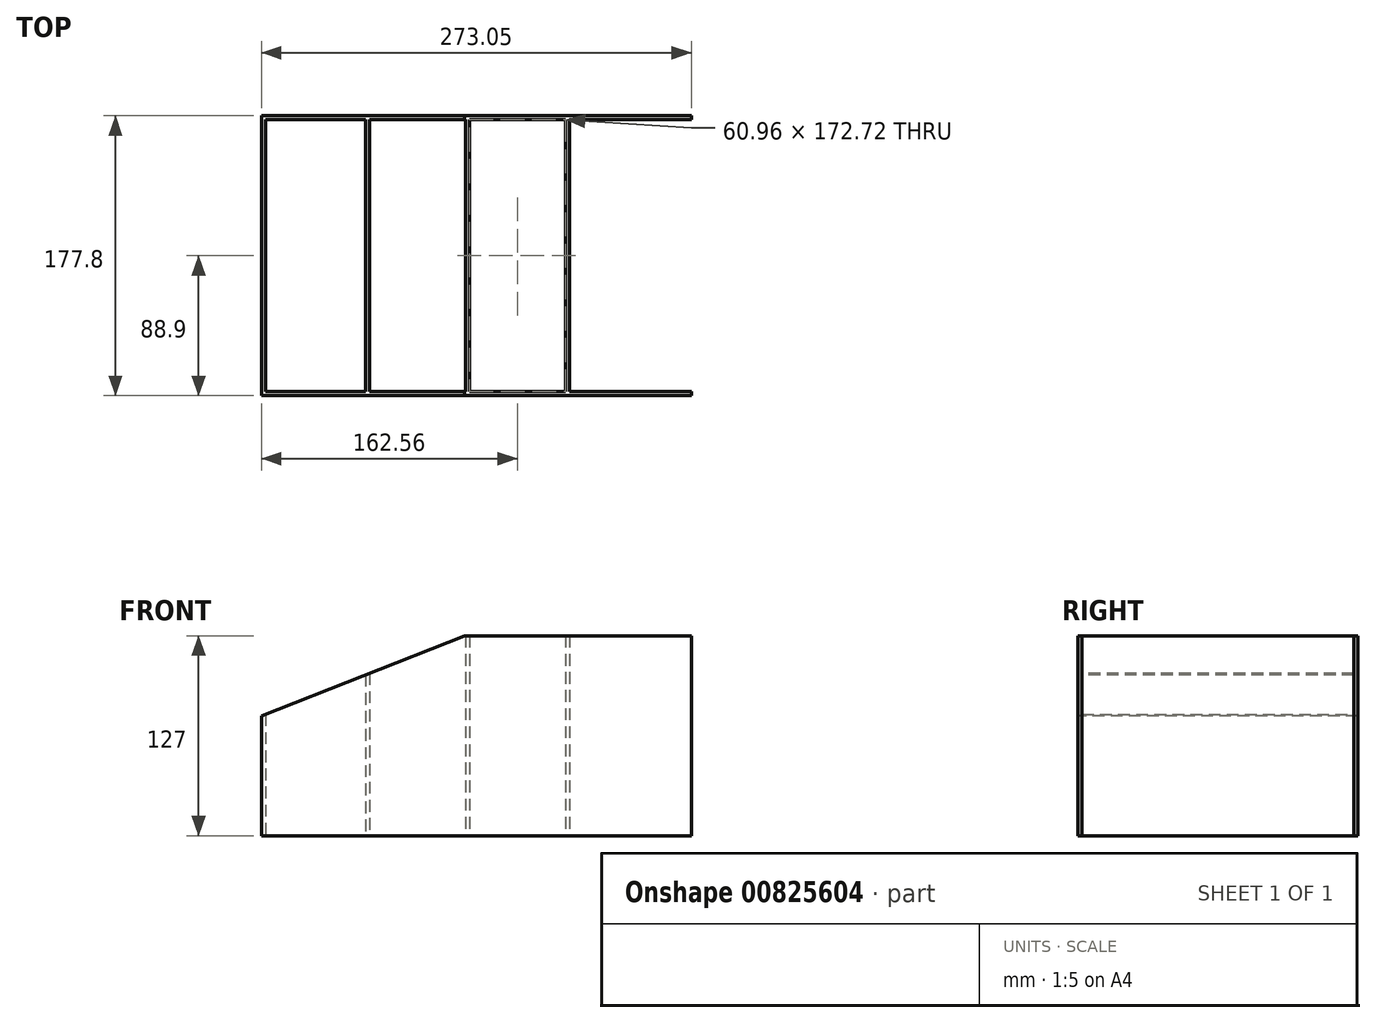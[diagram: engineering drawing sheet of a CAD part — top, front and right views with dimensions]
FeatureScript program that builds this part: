
annotation { "Feature Type Name" : "Feature", "Feature Type Description" : "" }
export const myFeature = defineFeature(function(context is Context, id is Id, definition is map)
    precondition{}
    {
        {
            var Q0;
            Q0=qCreatedBy(makeId("Top.planeOp"),FACE);
            var sketch = newSketch(context, id + "F0", { "sketchPlane" : qUnion([Q0])});
            skLineSegment(sketch, "E0.bottom", {"start": v(0, 0) * mm, "end": v(273.05, 0) * mm});
            skLineSegment(sketch, "E0.top", {"start": v(0, 177.8) * mm, "end": v(273.05, 177.8) * mm});
            skLineSegment(sketch, "E0.left", {"start": v(0, 0) * mm, "end": v(0, 177.8) * mm});
            skLineSegment(sketch, "E0.right", {"start": v(273.05, 0) * mm, "end": v(273.05, 177.8) * mm});
            skLineSegment(sketch, "E1.0", {"start": v(2.54, 175.26) * mm, "end": v(270.5, 175.26) * mm});
            skLineSegment(sketch, "E1.1", {"start": v(2.54, 2.54) * mm, "end": v(2.54, 175.26) * mm});
            skLineSegment(sketch, "E1.2", {"start": v(2.54, 2.54) * mm, "end": v(270.5, 2.54) * mm});
            skLineSegment(sketch, "E1.3", {"start": v(270.5, 2.54) * mm, "end": v(270.5, 175.26) * mm});
            skSolve(sketch);
        }
        {
            var Q0;
            Q0 = qSketchRegion(id + "F0", true);
            extrude(context, id + "F1", {"entities" : qUnion([Q0]), "depth" : 127 * mm, "offsetDistance" : 25.4 * mm});
        }
        {
            var Q0;
            Q0=qCreatedBy(makeId("Top.planeOp"),FACE);
            var sketch = newSketch(context, id + "F2", { "sketchPlane" : qUnion([Q0])});
            skLineSegment(sketch, "E2.bottom", {"start": v(66.04, 175.26) * mm, "end": v(68.58, 175.26) * mm});
            skLineSegment(sketch, "E2.top", {"start": v(66.04, 2.54) * mm, "end": v(68.58, 2.54) * mm});
            skLineSegment(sketch, "E2.left", {"start": v(66.04, 175.26) * mm, "end": v(66.04, 2.54) * mm});
            skLineSegment(sketch, "E2.right", {"start": v(68.58, 175.26) * mm, "end": v(68.58, 2.54) * mm});
            skLineSegment(sketch, "E3.1.0.0", {"start": v(132.08, 175.26) * mm, "end": v(132.08, 2.54) * mm});
            skLineSegment(sketch, "E3.1.0.1", {"start": v(129.54, 175.26) * mm, "end": v(129.54, 2.54) * mm});
            skLineSegment(sketch, "E3.1.0.2", {"start": v(129.54, 2.54) * mm, "end": v(132.08, 2.54) * mm});
            skLineSegment(sketch, "E3.1.0.3", {"start": v(129.54, 175.26) * mm, "end": v(132.08, 175.26) * mm});
            skLineSegment(sketch, "E3.2.0.0", {"start": v(195.58, 175.26) * mm, "end": v(195.58, 2.54) * mm});
            skLineSegment(sketch, "E3.2.0.1", {"start": v(193.04, 175.26) * mm, "end": v(193.04, 2.54) * mm});
            skLineSegment(sketch, "E3.2.0.2", {"start": v(193.04, 2.54) * mm, "end": v(195.58, 2.54) * mm});
            skLineSegment(sketch, "E3.2.0.3", {"start": v(193.04, 175.26) * mm, "end": v(195.58, 175.26) * mm});
            skLineSegment(sketch, "E3.direction1", {"start": v(66.04, 2.54) * mm, "end": v(129.54, 2.54) * mm, "construction": true});
            skSolve(sketch);
        }
        {
            var Q0;
            Q0 = qSketchRegion(id + "F2", true);
            extrude(context, id + "F3", {"entities" : qUnion([Q0]), "operationType" : NewBodyOperationType.ADD, "depth" : 127 * mm, "offsetDistance" : 25.4 * mm});
        }
        {
            var Q0;
            Q0=makeQuery(id+"F1.opExtrude","SWEPT_FACE",FACE,{"disambiguationData":[OSD([sQuery(id+"F0.wireOp",EDGE,"E0.bottom")])]});
            var sketch = newSketch(context, id + "F4", { "sketchPlane" : qUnion([Q0])});
            skLineSegment(sketch, "E4", {"start": v(128.84, 127) * mm, "end": v(0, 76.2) * mm});
            skLineSegment(sketch, "E5", {"start": v(0, 76.2) * mm, "end": v(0, 127) * mm});
            skLineSegment(sketch, "E6", {"start": v(0, 127) * mm, "end": v(128.84, 127) * mm});
            skPoint(sketch, "E7", {"position": v(136.53, 127) * mm});
            skSolve(sketch);
        }
        {
            var Q0;
            Q0 = qSketchRegion(id + "F4", true);
            extrude(context, id + "F5", {"entities" : qUnion([Q0]), "operationType" : NewBodyOperationType.REMOVE, "endBound" : BoundingType.THROUGH_ALL, "oppositeDirection" : true, "depth" : 25.4 * mm, "offsetDistance" : 25.4 * mm});
        }
        {
            var Q0;
            Q0=makeQuery(id+"F1.opExtrude","SWEPT_FACE",FACE,{"disambiguationData":[OSD([sQuery(id+"F0.wireOp",EDGE,"E0.right")])]});
            var sketch = newSketch(context, id + "F6", { "sketchPlane" : qUnion([Q0])});
            skLineSegment(sketch, "E8.bottom", {"start": v(2.54, 127) * mm, "end": v(175.26, 127) * mm});
            skLineSegment(sketch, "E8.top", {"start": v(2.54, 0) * mm, "end": v(175.26, 0) * mm});
            skLineSegment(sketch, "E8.left", {"start": v(2.54, 127) * mm, "end": v(2.54, 0) * mm});
            skLineSegment(sketch, "E8.right", {"start": v(175.26, 127) * mm, "end": v(175.26, 0) * mm});
            skSolve(sketch);
        }
        {
            var Q0;
            Q0 = qSketchRegion(id + "F6", true);
            extrude(context, id + "F7", {"entities" : qUnion([Q0]), "operationType" : NewBodyOperationType.REMOVE, "oppositeDirection" : true, "depth" : 25.4 * mm, "offsetDistance" : 25.4 * mm});
        }
    });
